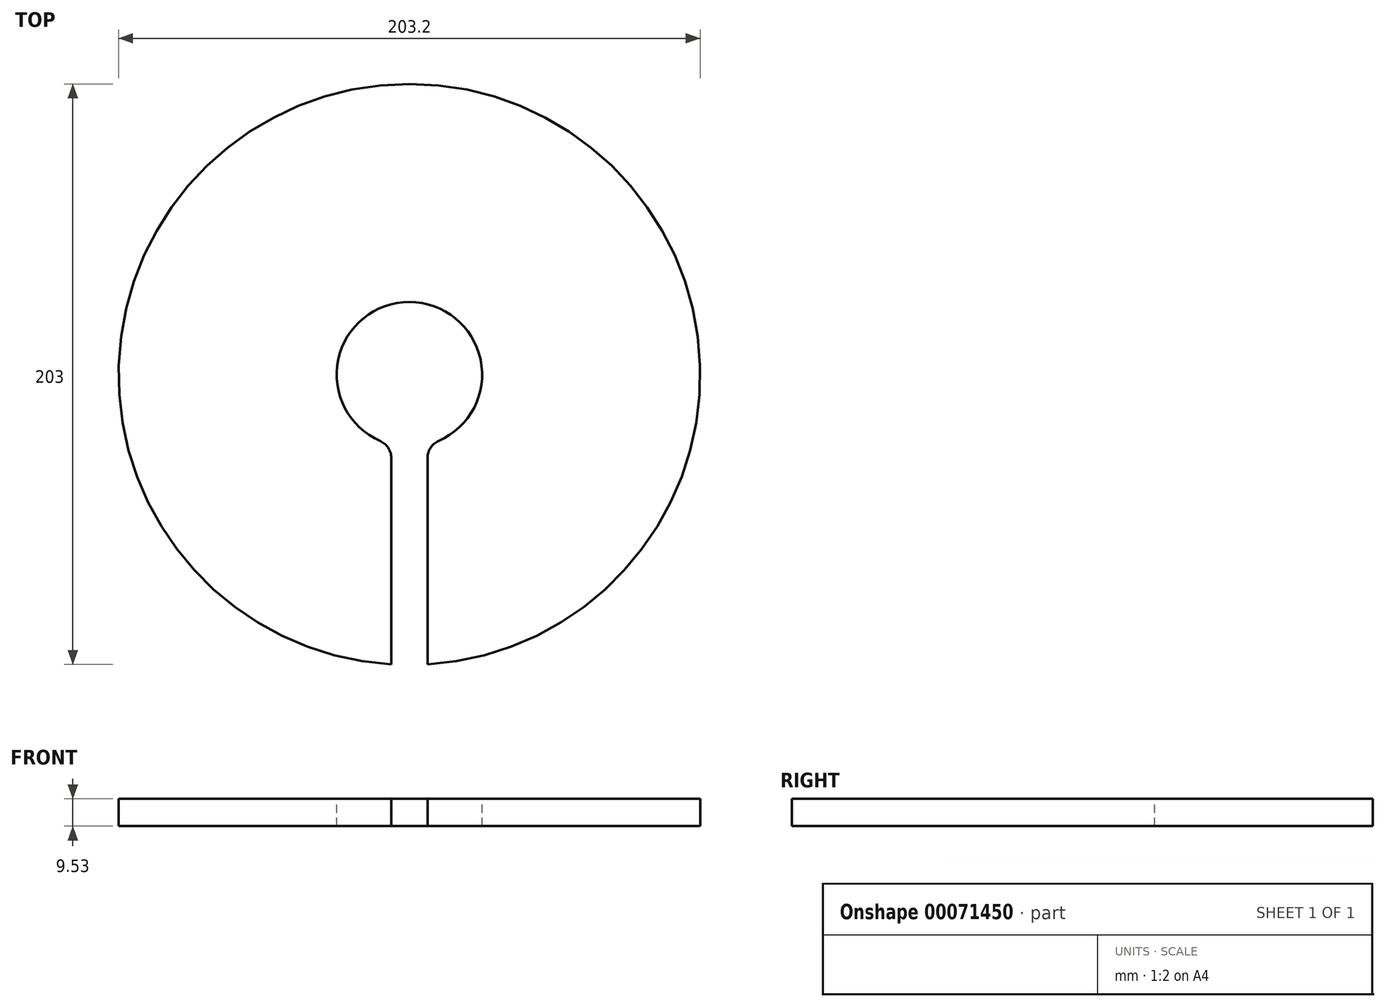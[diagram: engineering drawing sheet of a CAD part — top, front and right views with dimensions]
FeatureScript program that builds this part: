
annotation { "Feature Type Name" : "Feature", "Feature Type Description" : "" }
export const myFeature = defineFeature(function(context is Context, id is Id, definition is map)
    precondition{}
    {
        {
            var Q0;
            Q0=qCreatedBy(makeId("Top.planeOp"),FACE);
            var sketch = newSketch(context, id + "F0", { "sketchPlane" : qUnion([Q0])});
            skCircle(sketch, "E0", {"center": v(0, 0) * mm, "radius": 101.6 * mm});
            skSolve(sketch);
        }
        {
            var Q0;
            Q0 = qSketchRegion(id + "F0", true);
            extrude(context, id + "F1", {"entities" : qUnion([Q0]), "depth" : 9.52 * mm});
        }
        {
            var Q0;
            Q0=makeQuery(id+"F1.opExtrude","CAP_FACE",FACE,{"disambiguationData":[OSD([sQuery(id+"F0.wireOp",EDGE,"E0")])],"isStart":false});
            var sketch = newSketch(context, id + "F2", { "sketchPlane" : qUnion([Q0])});
            skArc(sketch, "E1", {"start": v(6.35, -24.6) * mm, "mid": v(0, 25.4) * mm, "end": v(-6.35, -24.6) * mm});
            skLineSegment(sketch, "E2", {"start": v(0, 101.6) * mm, "end": v(0, -101.6) * mm, "construction": true});
            skLineSegment(sketch, "E3", {"start": v(-6.35, -101.4) * mm, "end": v(-6.35, -24.6) * mm});
            skLineSegment(sketch, "E4", {"start": v(6.35, -101.4) * mm, "end": v(6.35, -24.6) * mm});
            skArc(sketch, "E5", {"start": v(-6.35, -101.4) * mm, "mid": v(0, -101.6) * mm, "end": v(6.35, -101.4) * mm});
            skSolve(sketch);
        }
        {
            var Q0;
            Q0 = qSketchRegion(id + "F2", true);
            extrude(context, id + "F3", {"entities" : qUnion([Q0]), "operationType" : NewBodyOperationType.REMOVE, "endBound" : BoundingType.THROUGH_ALL, "oppositeDirection" : true, "depth" : 25.4 * mm});
        }
        {
            var Q0;
            Q0=makeQuery(id+"F3.boolean.opBoolean","COPY",EDGE,{"derivedFrom":makeQuery(id+"F3.opExtrude","SWEPT_EDGE",EDGE,{"disambiguationData":[OSD([sQuery(id+"F0.wireOp",EDGE,"E0"),sQuery(id+"F2.wireOp",EDGE,"E3"),sQuery(id+"F2.wireOp",EDGE,"E5")])]})});
            var Q1;
            Q1=makeQuery(id+"F3.boolean.opBoolean","COPY",EDGE,{"derivedFrom":makeQuery(id+"F3.opExtrude","SWEPT_EDGE",EDGE,{"disambiguationData":[OSD([sQuery(id+"F0.wireOp",EDGE,"E0"),sQuery(id+"F2.wireOp",EDGE,"E4"),sQuery(id+"F2.wireOp",EDGE,"E5")])]})});
            var Q2;
            Q2=makeQuery(id+"F3.boolean.opBoolean","COPY",EDGE,{"derivedFrom":makeQuery(id+"F3.opExtrude","SWEPT_EDGE",EDGE,{"disambiguationData":[OSD([sQuery(id+"F2.wireOp",EDGE,"E1"),sQuery(id+"F2.wireOp",EDGE,"E3")])]})});
            var Q3;
            Q3=makeQuery(id+"F3.boolean.opBoolean","COPY",EDGE,{"derivedFrom":makeQuery(id+"F3.opExtrude","SWEPT_EDGE",EDGE,{"disambiguationData":[OSD([sQuery(id+"F2.wireOp",EDGE,"E1"),sQuery(id+"F2.wireOp",EDGE,"E4")])]})});
            fillet(context, id + "F4", {"entities" : qUnion([Q0, Q1, Q2, Q3]), "radius" : 6.35 * mm, "tangentPropagation" : true, "allowEdgeOverflow" : false});
        }
    });
